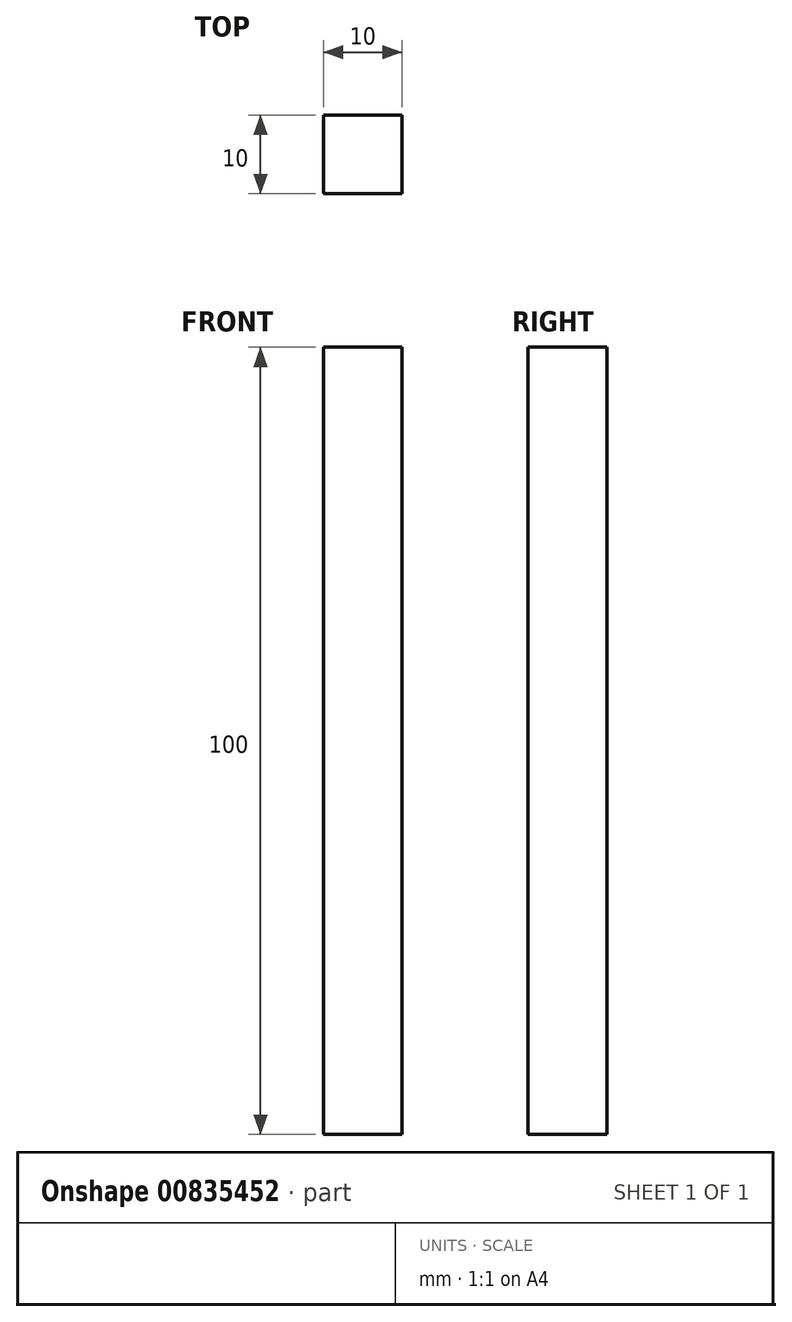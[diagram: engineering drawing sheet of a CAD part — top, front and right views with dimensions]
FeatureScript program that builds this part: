
annotation { "Feature Type Name" : "Feature", "Feature Type Description" : "" }
export const myFeature = defineFeature(function(context is Context, id is Id, definition is map)
    precondition{}
    {
        {
            var Q0;
            Q0=qCreatedBy(makeId("Top.planeOp"),FACE);
            var sketch = newSketch(context, id + "F0", { "sketchPlane" : qUnion([Q0])});
            skLineSegment(sketch, "E0.bottom", {"start": v(5, -5) * mm, "end": v(-5, -5) * mm});
            skLineSegment(sketch, "E0.top", {"start": v(5, 5) * mm, "end": v(-5, 5) * mm});
            skLineSegment(sketch, "E0.left", {"start": v(5, -5) * mm, "end": v(5, 5) * mm});
            skLineSegment(sketch, "E0.right", {"start": v(-5, -5) * mm, "end": v(-5, 5) * mm});
            skPoint(sketch, "E0.middle", {"position": v(0, 0) * mm});
            skSolve(sketch);
        }
        {
            var Q0;
            Q0 = qSketchRegion(id + "F0", true);
            extrude(context, id + "F1", {"entities" : qUnion([Q0]), "depth" : 100 * mm, "offsetDistance" : 25 * mm});
        }
    });
